# Revit family: SF_Ohm
name_source: partatom
category: Structural Framing
units: mm (PartAtom-declared; Revit-internal decimal feet)

## family parameters
Always export as geometry = No
Always vertical = Yes
Cut with Voids When Loaded = No
Material for Model Behavior = Other
OmniClass Number = 23.25.30.11.14.14
OmniClass Title = Beams
Section Shape = Not Defined
Shared = No
Show family pre-cut in plan views = Yes

## types (28) — shared parameters
A = 89 mm
D = 18 mm
D2 = 18 mm
R = 10 mm

## per-type parameters (varying)
| type | B | e |
| Ohm 400x6 | 400 mm | 6 mm |
| Ohm 400x5 | 400 mm | 5 mm |
| Ohm 400x4 | 400 mm | 4 mm |
| Ohm 400x3 | 400 mm | 3 mm |
| Ohm 350x6 | 350 mm | 6 mm |
| Ohm 350x5 | 350 mm | 5 mm |
| Ohm 350x4 | 350 mm | 4 mm |
| Ohm 350x3 | 350 mm | 3 mm |
| Ohm 300x6 | 300 mm | 6 mm |
| Ohm 300x5 | 300 mm | 5 mm |
| Ohm 300x4 | 300 mm | 4 mm |
| Ohm 300x3 | 300 mm | 3 mm |
| Ohm 250x6 | 250 mm | 6 mm |
| Ohm 250x5 | 250 mm | 5 mm |
| Ohm 250x4 | 250 mm | 4 mm |
| Ohm 250x3 | 250 mm | 3 mm |
| Ohm 225x6 | 225 mm | 6 mm |
| Ohm 225x5 | 225 mm | 5 mm |
| Ohm 225x4 | 225 mm | 4 mm |
| Ohm 225x3 | 225 mm | 3 mm |
| Ohm 200x6 | 200 mm | 6 mm |
| Ohm 200x5 | 200 mm | 5 mm |
| Ohm 200x4 | 200 mm | 4 mm |
| Ohm 200x3 | 200 mm | 3 mm |
| Ohm 150x6 | 150 mm | 6 mm |
| Ohm 150x5 | 150 mm | 5 mm |
| Ohm 150x4 | 150 mm | 4 mm |
| Ohm 150x3 | 150 mm | 3 mm |

## geometry (parser evidence)
native form markers: Blend x2, Sweep x3
no freeform markers — native parametric forms only
